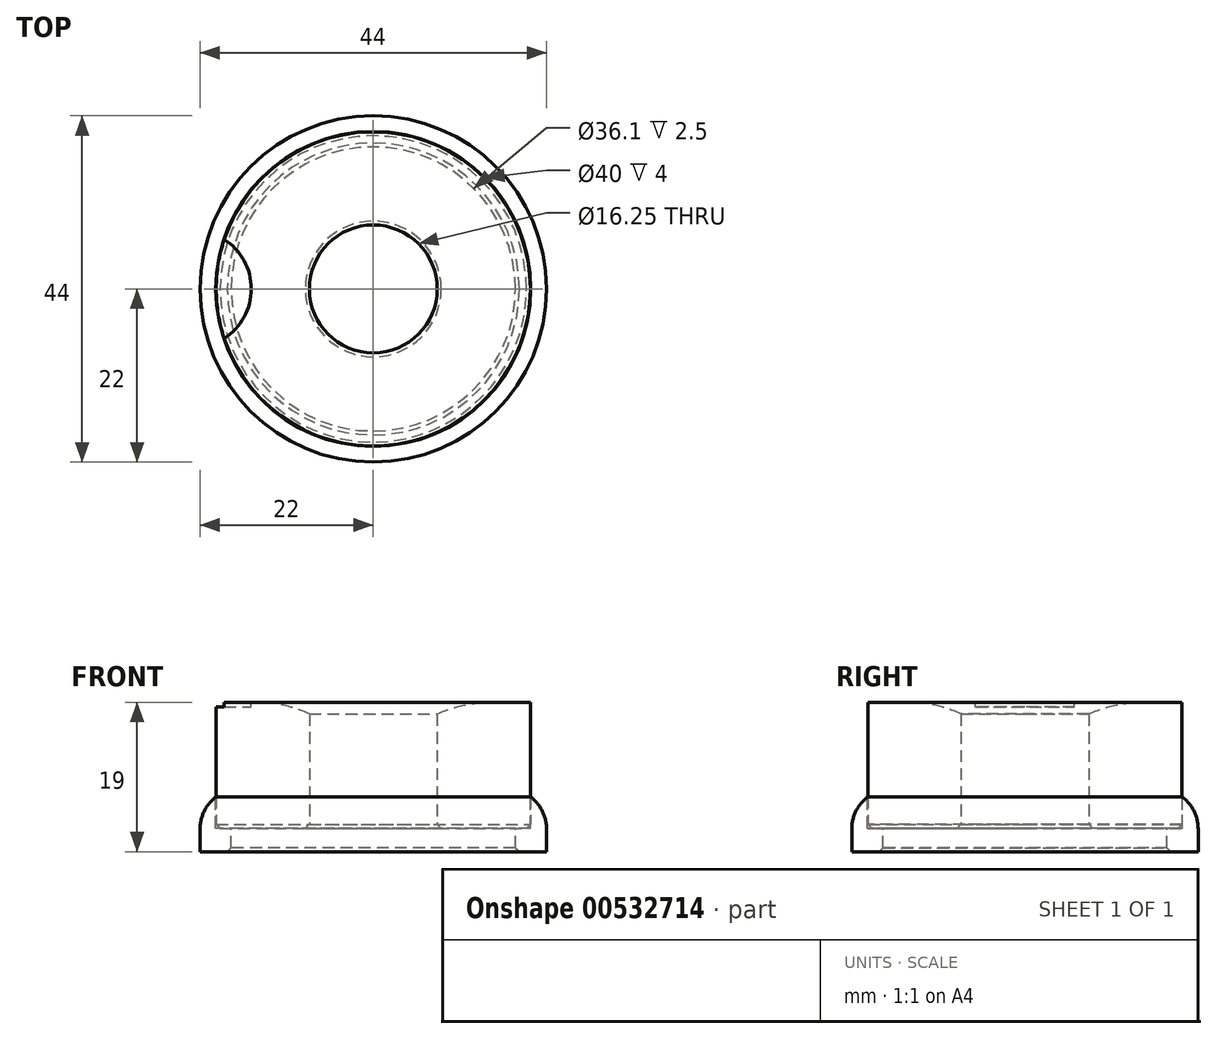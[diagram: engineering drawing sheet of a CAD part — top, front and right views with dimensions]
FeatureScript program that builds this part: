
annotation { "Feature Type Name" : "Feature", "Feature Type Description" : "" }
export const myFeature = defineFeature(function(context is Context, id is Id, definition is map)
    precondition{}
    {
        {
            var Q0;
            Q0=qCreatedBy(makeId("Front.planeOp"),FACE);
            var sketch = newSketch(context, id + "F0", { "sketchPlane" : qUnion([Q0])});
            skLineSegment(sketch, "E0", {"start": v(0, 0) * mm, "end": v(0, 98.82) * mm, "construction": true});
            skLineSegment(sketch, "E1", {"start": v(8.13, 0) * mm, "end": v(19.95, 0) * mm});
            skLineSegment(sketch, "E2", {"start": v(19.95, 0) * mm, "end": v(19.95, 16) * mm});
            skLineSegment(sketch, "E3", {"start": v(8.13, 14.5) * mm, "end": v(8.13, 0) * mm});
            skLineSegment(sketch, "E4", {"start": v(19.95, 16) * mm, "end": v(15, 16) * mm});
            skArc(sketch, "E5", {"start": v(15, 16) * mm, "mid": v(11.48, 15.62) * mm, "end": v(8.13, 14.5) * mm});
            skSolve(sketch);
        }
        {
            var Q0;
            Q0=makeQuery(id+"F0.imprint","IMPRINT",FACE,{"disambiguationData":[TD([[makeQuery(id+"F0.imprint","IMPRINT",EDGE,{"derivedFrom":sQuery(id+"F0.wireOp",EDGE,"E1")}),1.0]])]});
            var Q1;
            Q1=sQuery(id+"F0.wireOp",EDGE,"E0");
            revolve(context, id + "F1", {"entities" : qUnion([Q0]), "axis" : qUnion([Q1]), "revolveType" : RevolveType.FULL});
        }
        {
            var Q0;
            Q0=qCreatedBy(makeId("Front.planeOp"),FACE);
            var sketch = newSketch(context, id + "F2", { "sketchPlane" : qUnion([Q0])});
            skLineSegment(sketch, "E6", {"start": v(18.05, 0) * mm, "end": v(18.05, -3) * mm});
            skLineSegment(sketch, "E7", {"start": v(18.05, -3) * mm, "end": v(22, -3) * mm});
            skLineSegment(sketch, "E8", {"start": v(22, -3) * mm, "end": v(22, 2) * mm});
            skLineSegment(sketch, "E9", {"start": v(22, 2) * mm, "end": v(20, 4) * mm});
            skLineSegment(sketch, "E10", {"start": v(20, 4) * mm, "end": v(20, 0) * mm});
            skLineSegment(sketch, "E11", {"start": v(20, 0) * mm, "end": v(18.05, 0) * mm});
            skLineSegment(sketch, "E12", {"start": v(0, 0) * mm, "end": v(0, -14.33) * mm, "construction": true});
            skSolve(sketch);
        }
        {
            var Q0;
            Q0 = qSketchRegion(id + "F2", true);
            var Q1;
            Q1=sQuery(id+"F2.wireOp",EDGE,"E12");
            revolve(context, id + "F3", {"entities" : qUnion([Q0]), "axis" : qUnion([Q1]), "revolveType" : RevolveType.FULL});
        }
        {
            var Q0;
            Q0=makeQuery(id+"F1.opRevolve","SWEPT_FACE",FACE,{"disambiguationData":[OSD([sQuery(id+"F0.wireOp",EDGE,"E4")])]});
            var sketch = newSketch(context, id + "F4", { "sketchPlane" : qUnion([Q0])});
            skCircle(sketch, "E13", {"center": v(-23, 0) * mm, "radius": 7.5 * mm});
            skSolve(sketch);
        }
        {
            var Q0;
            Q0 = qSketchRegion(id + "F4", true);
            extrude(context, id + "F5", {"entities" : qUnion([Q0]), "operationType" : NewBodyOperationType.REMOVE, "oppositeDirection" : true, "depth" : 0.6 * mm, "offsetDistance" : 25 * mm});
        }
        {
            var Q0;
            Q0=makeQuery(id+"F3.opRevolve","SWEPT_EDGE",EDGE,{"disambiguationData":[OSD([sQuery(id+"F2.wireOp",EDGE,"E8"),sQuery(id+"F2.wireOp",EDGE,"E9")])]});
            fillet(context, id + "F6", {"entities" : qUnion([Q0]), "radius" : 5 * mm, "tangentPropagation" : true, "allowEdgeOverflow" : false});
        }
        {
            var Q0;
            Q0=makeQuery(id+"F3.opRevolve","SWEPT_EDGE",EDGE,{"disambiguationData":[OSD([sQuery(id+"F2.wireOp",EDGE,"E6"),sQuery(id+"F2.wireOp",EDGE,"E7")])]});
            chamfer(context, id + "F7", {"entities" : qUnion([Q0]), "width" : 0.5 * mm, "tangentPropagation" : true});
        }
        {
            var Q0;
            Q0=makeQuery(id+"F1.opRevolve","SWEPT_EDGE",EDGE,{"disambiguationData":[OSD([sQuery(id+"F0.wireOp",EDGE,"E1"),sQuery(id+"F0.wireOp",EDGE,"E2")])]});
            var Q1;
            Q1=makeQuery(id+"F1.opRevolve","SWEPT_EDGE",EDGE,{"disambiguationData":[OSD([sQuery(id+"F0.wireOp",EDGE,"E1"),sQuery(id+"F0.wireOp",EDGE,"E3")])]});
            chamfer(context, id + "F8", {"entities" : qUnion([Q0, Q1]), "width" : 0.5 * mm, "tangentPropagation" : true});
        }
    });
